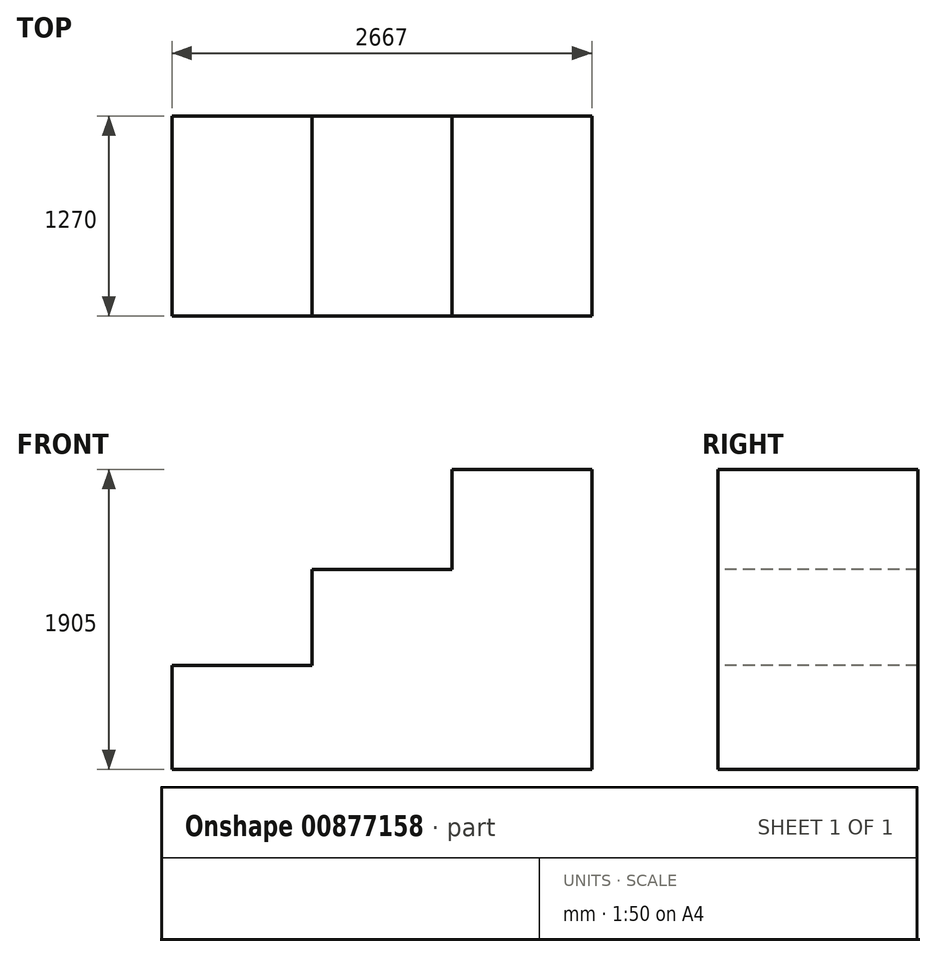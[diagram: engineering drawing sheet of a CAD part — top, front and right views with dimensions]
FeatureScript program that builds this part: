
annotation { "Feature Type Name" : "Feature", "Feature Type Description" : "" }
export const myFeature = defineFeature(function(context is Context, id is Id, definition is map)
    precondition{}
    {
        {
            var Q0;
            Q0=qCreatedBy(makeId("Top.planeOp"),FACE);
            var sketch = newSketch(context, id + "F0", { "sketchPlane" : qUnion([Q0])});
            skLineSegment(sketch, "E0.bottom", {"start": v(0, 0) * mm, "end": v(2667, 0) * mm});
            skLineSegment(sketch, "E0.top", {"start": v(0, -1270) * mm, "end": v(2667, -1270) * mm});
            skLineSegment(sketch, "E0.left", {"start": v(0, 0) * mm, "end": v(0, -1270) * mm});
            skLineSegment(sketch, "E0.right", {"start": v(2667, 0) * mm, "end": v(2667, -1270) * mm});
            skSolve(sketch);
        }
        {
            var Q0;
            Q0 = qSketchRegion(id + "F0", true);
            extrude(context, id + "F1", {"entities" : qUnion([Q0]), "depth" : 635 * mm, "offsetDistance" : 25.4 * mm});
        }
        {
            var Q0;
            Q0=makeQuery(id+"F1.opExtrude","CAP_FACE",FACE,{"disambiguationData":[OSD([sQuery(id+"F0.wireOp",EDGE,"E0.bottom"),sQuery(id+"F0.wireOp",EDGE,"E0.top"),sQuery(id+"F0.wireOp",EDGE,"E0.left"),sQuery(id+"F0.wireOp",EDGE,"E0.right")])],"isStart":false});
            var sketch = newSketch(context, id + "F2", { "sketchPlane" : qUnion([Q0])});
            skLineSegment(sketch, "E1.bottom", {"start": v(0, 0) * mm, "end": v(889, 0) * mm});
            skLineSegment(sketch, "E1.top", {"start": v(0, -1270) * mm, "end": v(889, -1270) * mm});
            skLineSegment(sketch, "E1.left", {"start": v(0, 0) * mm, "end": v(0, -1270) * mm});
            skLineSegment(sketch, "E1.right", {"start": v(889, 0) * mm, "end": v(889, -1270) * mm});
            skSolve(sketch);
        }
        {
            var Q0;
            Q0 = qSketchRegion(id + "F2", true);
            extrude(context, id + "F3", {"entities" : qUnion([Q0]), "operationType" : NewBodyOperationType.ADD, "depth" : 25.4 * mm, "offsetDistance" : 25.4 * mm});
        }
        {
            var Q0;
            Q0=makeQuery(id+"F1.opExtrude","CAP_FACE",FACE,{"disambiguationData":[OSD([sQuery(id+"F0.wireOp",EDGE,"E0.bottom"),sQuery(id+"F0.wireOp",EDGE,"E0.top"),sQuery(id+"F0.wireOp",EDGE,"E0.left"),sQuery(id+"F0.wireOp",EDGE,"E0.right")])],"isStart":false});
            var sketch = newSketch(context, id + "F4", { "sketchPlane" : qUnion([Q0])});
            skLineSegment(sketch, "E2.bottom", {"start": v(889, 0) * mm, "end": v(1778, 0) * mm});
            skLineSegment(sketch, "E2.top", {"start": v(889, -1270) * mm, "end": v(1778, -1270) * mm});
            skLineSegment(sketch, "E2.left", {"start": v(889, 0) * mm, "end": v(889, -1270) * mm});
            skLineSegment(sketch, "E2.right", {"start": v(1778, 0) * mm, "end": v(1778, -1270) * mm});
            skSolve(sketch);
        }
        {
            var Q0;
            Q0=makeQuery(id+"F4.imprint","IMPRINT",FACE,{"disambiguationData":[TD([[makeQuery(id+"F4.imprint","IMPRINT",EDGE,{"derivedFrom":sQuery(id+"F4.wireOp",EDGE,"E2.bottom")}),-1.0]])]});
            extrude(context, id + "F5", {"entities" : qUnion([Q0]), "operationType" : NewBodyOperationType.ADD, "depth" : 635 * mm, "offsetDistance" : 25.4 * mm});
        }
        {
            var Q0;
            Q0=makeQuery(id+"F1.opExtrude","CAP_FACE",FACE,{"disambiguationData":[OSD([sQuery(id+"F0.wireOp",EDGE,"E0.bottom"),sQuery(id+"F0.wireOp",EDGE,"E0.top"),sQuery(id+"F0.wireOp",EDGE,"E0.left"),sQuery(id+"F0.wireOp",EDGE,"E0.right")])],"isStart":false});
            var sketch = newSketch(context, id + "F6", { "sketchPlane" : qUnion([Q0])});
            skLineSegment(sketch, "E3.bottom", {"start": v(1778, 0) * mm, "end": v(2667, 0) * mm});
            skLineSegment(sketch, "E3.top", {"start": v(1778, -1270) * mm, "end": v(2667, -1270) * mm});
            skLineSegment(sketch, "E3.left", {"start": v(1778, 0) * mm, "end": v(1778, -1270) * mm});
            skLineSegment(sketch, "E3.right", {"start": v(2667, 0) * mm, "end": v(2667, -1270) * mm});
            skSolve(sketch);
        }
        {
            var Q0;
            Q0=makeQuery(id+"F6.imprint","IMPRINT",FACE,{"disambiguationData":[TD([[makeQuery(id+"F6.imprint","IMPRINT",EDGE,{"derivedFrom":sQuery(id+"F6.wireOp",EDGE,"E3.bottom")}),-1.0]])]});
            extrude(context, id + "F7", {"entities" : qUnion([Q0]), "operationType" : NewBodyOperationType.ADD, "depth" : 1270 * mm, "offsetDistance" : 25.4 * mm});
        }
    });
